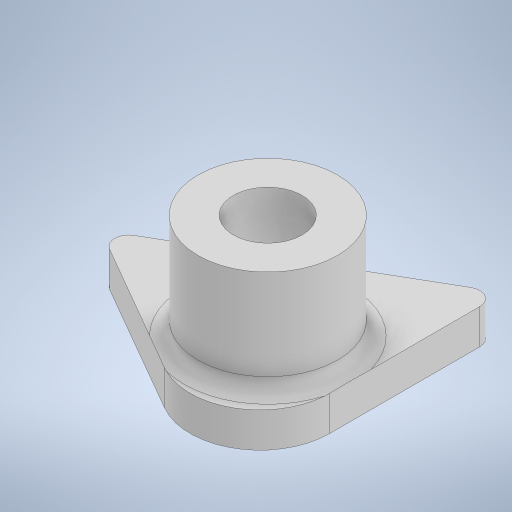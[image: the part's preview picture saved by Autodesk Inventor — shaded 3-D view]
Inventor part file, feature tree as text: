
AUTODESK INVENTOR PART (.ipt)
format: ipt  version: 2023 (Build 270158000, 158)  size: 271,872 bytes
history: native  units: in
note: dims shown in document units (in); Inventor stores cm internally (conversion verified against a paired STEP export)
features: other x4, extrude x1, sketch x1
ambient origin geometry x8: Origin, YZ Plane, XZ Plane, XY Plane, X Axis, Y Axis, Z Axis, Center Point
bodies: Body1 (feature_tree)
feature tree (6):
  other  "base.ipt"
  extrude  "Extrusion1"  Depth=0.3937in
  other  "Tight_Bushing::base.ipt"
  other  "TaggingFeature1"
  sketch  "Sketch1"  dims[d0=0.3937in d1=0.3882in d2=1.0in d3=0.0in]
  other  "Tight_Bushing"
